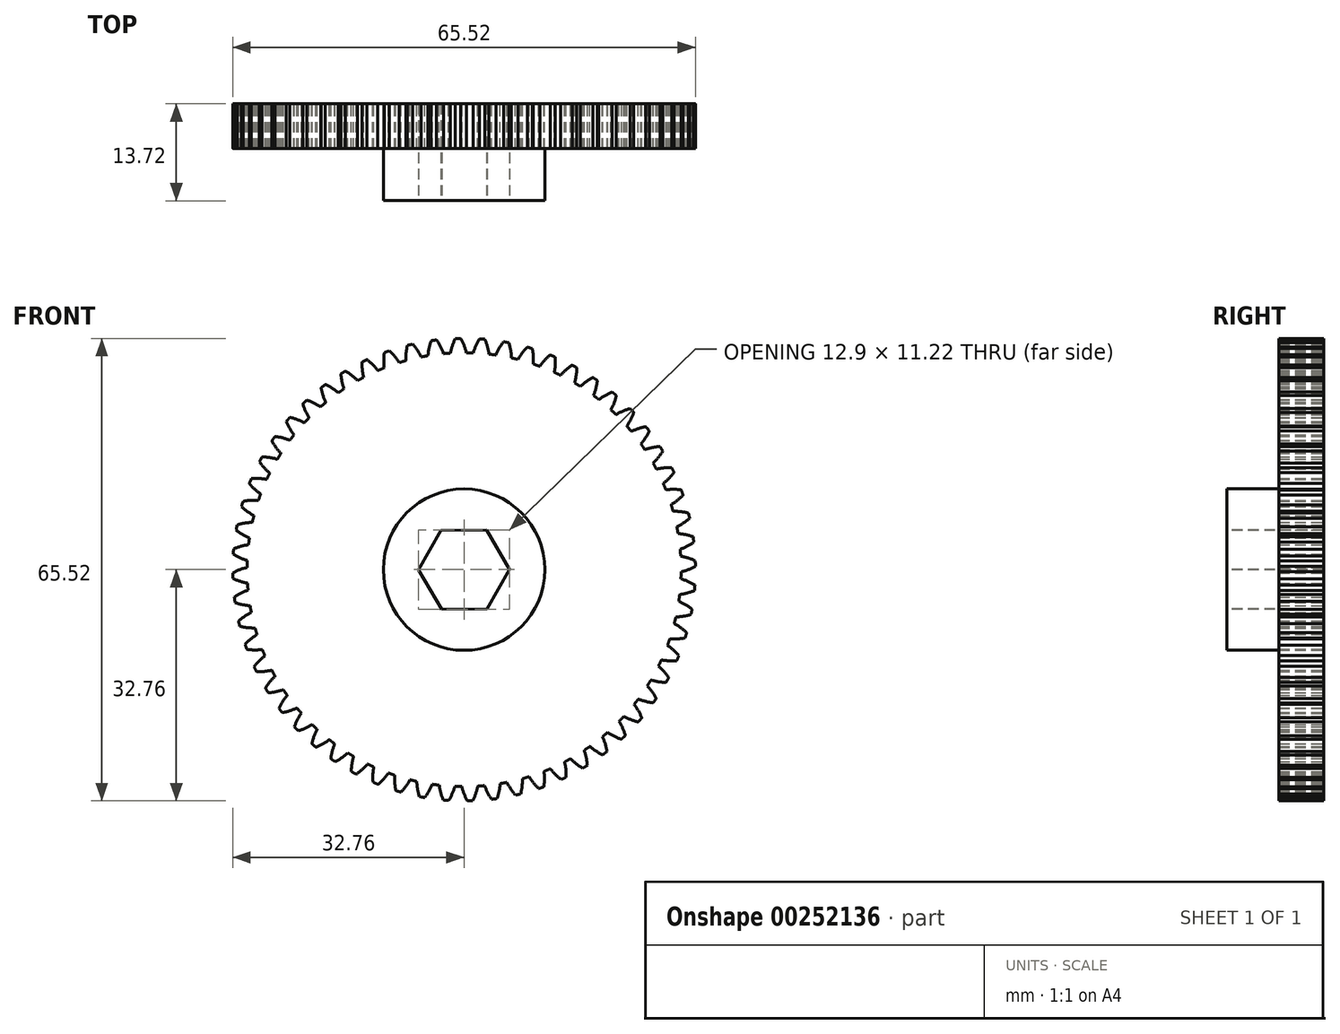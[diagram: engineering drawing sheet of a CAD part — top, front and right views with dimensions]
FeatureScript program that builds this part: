
annotation { "Feature Type Name" : "Feature", "Feature Type Description" : "" }
export const myFeature = defineFeature(function(context is Context, id is Id, definition is map)
    precondition{}
    {
        {
            var Q0;
            Q0=qCreatedBy(makeId("Front.planeOp"),FACE);
            var sketch = newSketch(context, id + "F0", { "sketchPlane" : qUnion([Q0])});
            skArc(sketch, "E0", {"start": v(-0.47, 32.76) * mm, "mid": v(-0.67, 32.76) * mm, "end": v(-0.86, 32.75) * mm});
            skArc(sketch, "E1", {"start": v(1.3, 30.7) * mm, "mid": v(0.8, 30.72) * mm, "end": v(0.31, 30.73) * mm});
            skArc(sketch, "E2.trimOffspring", {"start": v(0.31, 30.73) * mm, "mid": v(0, 31.77) * mm, "end": v(-0.47, 32.76) * mm});
            skArc(sketch, "E3.MirrorCS", {"start": v(-1.24, 32.74) * mm, "mid": v(-1.05, 32.75) * mm, "end": v(-0.86, 32.75) * mm});
            skArc(sketch, "E4.MirrorCS", {"start": v(-1.92, 30.67) * mm, "mid": v(-1.65, 31.73) * mm, "end": v(-1.24, 32.74) * mm});
            skArc(sketch, "E5.1.0", {"start": v(-5.12, 30.3) * mm, "mid": v(-4.96, 31.38) * mm, "end": v(-4.66, 32.43) * mm});
            skArc(sketch, "E5.1.1", {"start": v(-4.66, 32.43) * mm, "mid": v(-4.47, 32.46) * mm, "end": v(-4.28, 32.49) * mm});
            skArc(sketch, "E5.1.2", {"start": v(-3.9, 32.53) * mm, "mid": v(-4.09, 32.51) * mm, "end": v(-4.28, 32.49) * mm});
            skArc(sketch, "E5.1.3", {"start": v(-2.9, 30.6) * mm, "mid": v(-3.33, 31.6) * mm, "end": v(-3.9, 32.53) * mm});
            skArc(sketch, "E5.2.0", {"start": v(-8.26, 29.6) * mm, "mid": v(-8.21, 30.7) * mm, "end": v(-8.02, 31.77) * mm});
            skArc(sketch, "E5.2.1", {"start": v(-8.02, 31.77) * mm, "mid": v(-7.84, 31.82) * mm, "end": v(-7.65, 31.86) * mm});
            skArc(sketch, "E5.2.2", {"start": v(-7.28, 31.95) * mm, "mid": v(-7.46, 31.9) * mm, "end": v(-7.65, 31.86) * mm});
            skArc(sketch, "E5.2.3", {"start": v(-6.08, 30.13) * mm, "mid": v(-6.62, 31.08) * mm, "end": v(-7.28, 31.95) * mm});
            skArc(sketch, "E5.3.0", {"start": v(-11.3, 28.58) * mm, "mid": v(-11.38, 29.67) * mm, "end": v(-11.3, 30.76) * mm});
            skArc(sketch, "E5.3.1", {"start": v(-11.3, 30.76) * mm, "mid": v(-11.12, 30.82) * mm, "end": v(-10.94, 30.89) * mm});
            skArc(sketch, "E5.3.2", {"start": v(-10.57, 31.01) * mm, "mid": v(-10.76, 30.95) * mm, "end": v(-10.94, 30.89) * mm});
            skArc(sketch, "E5.3.3", {"start": v(-9.2, 29.33) * mm, "mid": v(-9.83, 30.22) * mm, "end": v(-10.57, 31.01) * mm});
            skArc(sketch, "E5.4.0", {"start": v(-14.23, 27.24) * mm, "mid": v(-14.42, 28.32) * mm, "end": v(-14.45, 29.4) * mm});
            skArc(sketch, "E5.4.1", {"start": v(-14.45, 29.4) * mm, "mid": v(-14.28, 29.5) * mm, "end": v(-14.1, 29.57) * mm});
            skArc(sketch, "E5.4.2", {"start": v(-13.76, 29.74) * mm, "mid": v(-13.93, 29.66) * mm, "end": v(-14.1, 29.57) * mm});
            skArc(sketch, "E5.4.3", {"start": v(-12.21, 28.2) * mm, "mid": v(-12.93, 29.02) * mm, "end": v(-13.76, 29.74) * mm});
            skArc(sketch, "E5.5.0", {"start": v(-17, 25.6) * mm, "mid": v(-17.3, 26.65) * mm, "end": v(-17.45, 27.74) * mm});
            skArc(sketch, "E5.5.1", {"start": v(-17.45, 27.74) * mm, "mid": v(-17.28, 27.84) * mm, "end": v(-17.12, 27.94) * mm});
            skArc(sketch, "E5.5.2", {"start": v(-16.8, 28.14) * mm, "mid": v(-16.96, 28.04) * mm, "end": v(-17.12, 27.94) * mm});
            skArc(sketch, "E5.5.3", {"start": v(-15.1, 26.77) * mm, "mid": v(-15.9, 27.51) * mm, "end": v(-16.8, 28.14) * mm});
            skArc(sketch, "E5.6.0", {"start": v(-19.59, 23.69) * mm, "mid": v(-19.99, 24.7) * mm, "end": v(-20.25, 25.76) * mm});
            skArc(sketch, "E5.6.1", {"start": v(-20.25, 25.76) * mm, "mid": v(-20.1, 25.88) * mm, "end": v(-19.95, 26) * mm});
            skArc(sketch, "E5.6.2", {"start": v(-19.64, 26.23) * mm, "mid": v(-19.8, 26.11) * mm, "end": v(-19.95, 26) * mm});
            skArc(sketch, "E5.6.3", {"start": v(-17.8, 25.05) * mm, "mid": v(-18.68, 25.7) * mm, "end": v(-19.64, 26.23) * mm});
            skArc(sketch, "E5.7.0", {"start": v(-21.95, 21.5) * mm, "mid": v(-22.46, 22.47) * mm, "end": v(-22.83, 23.5) * mm});
            skArc(sketch, "E5.7.1", {"start": v(-22.83, 23.5) * mm, "mid": v(-22.7, 23.64) * mm, "end": v(-22.55, 23.77) * mm});
            skArc(sketch, "E5.7.2", {"start": v(-22.27, 24.03) * mm, "mid": v(-22.41, 23.9) * mm, "end": v(-22.55, 23.77) * mm});
            skArc(sketch, "E5.7.3", {"start": v(-20.33, 23.05) * mm, "mid": v(-21.27, 23.6) * mm, "end": v(-22.27, 24.03) * mm});
            skArc(sketch, "E5.8.0", {"start": v(-24.08, 19.1) * mm, "mid": v(-24.69, 20) * mm, "end": v(-25.16, 20.99) * mm});
            skArc(sketch, "E5.8.1", {"start": v(-25.16, 20.99) * mm, "mid": v(-25.04, 21.13) * mm, "end": v(-24.92, 21.28) * mm});
            skArc(sketch, "E5.8.2", {"start": v(-24.66, 21.57) * mm, "mid": v(-24.8, 21.43) * mm, "end": v(-24.92, 21.28) * mm});
            skArc(sketch, "E5.8.3", {"start": v(-22.63, 20.8) * mm, "mid": v(-23.62, 21.25) * mm, "end": v(-24.66, 21.57) * mm});
            skArc(sketch, "E5.9.0", {"start": v(-25.95, 16.47) * mm, "mid": v(-26.64, 17.31) * mm, "end": v(-27.22, 18.24) * mm});
            skArc(sketch, "E5.9.1", {"start": v(-27.22, 18.24) * mm, "mid": v(-27.11, 18.4) * mm, "end": v(-27, 18.56) * mm});
            skArc(sketch, "E5.9.2", {"start": v(-26.78, 18.87) * mm, "mid": v(-26.9, 18.72) * mm, "end": v(-27, 18.56) * mm});
            skArc(sketch, "E5.9.3", {"start": v(-24.68, 18.32) * mm, "mid": v(-25.71, 18.67) * mm, "end": v(-26.78, 18.87) * mm});
            skArc(sketch, "E5.10.0", {"start": v(-27.53, 13.67) * mm, "mid": v(-28.3, 14.43) * mm, "end": v(-28.98, 15.3) * mm});
            skArc(sketch, "E5.10.1", {"start": v(-28.98, 15.3) * mm, "mid": v(-28.89, 15.47) * mm, "end": v(-28.8, 15.63) * mm});
            skArc(sketch, "E5.10.2", {"start": v(-28.61, 15.97) * mm, "mid": v(-28.7, 15.8) * mm, "end": v(-28.8, 15.63) * mm});
            skArc(sketch, "E5.10.3", {"start": v(-26.46, 15.64) * mm, "mid": v(-27.52, 15.88) * mm, "end": v(-28.61, 15.97) * mm});
            skArc(sketch, "E5.11.0", {"start": v(-28.8, 10.72) * mm, "mid": v(-29.66, 11.4) * mm, "end": v(-30.42, 12.18) * mm});
            skArc(sketch, "E5.11.1", {"start": v(-30.42, 12.18) * mm, "mid": v(-30.34, 12.36) * mm, "end": v(-30.27, 12.54) * mm});
            skArc(sketch, "E5.11.2", {"start": v(-30.12, 12.9) * mm, "mid": v(-30.2, 12.72) * mm, "end": v(-30.27, 12.54) * mm});
            skArc(sketch, "E5.11.3", {"start": v(-27.95, 12.79) * mm, "mid": v(-29.03, 12.92) * mm, "end": v(-30.12, 12.9) * mm});
            skArc(sketch, "E5.12.0", {"start": v(-29.77, 7.65) * mm, "mid": v(-30.69, 8.23) * mm, "end": v(-31.52, 8.94) * mm});
            skArc(sketch, "E5.12.1", {"start": v(-31.52, 8.94) * mm, "mid": v(-31.47, 9.12) * mm, "end": v(-31.42, 9.3) * mm});
            skArc(sketch, "E5.12.2", {"start": v(-31.3, 9.67) * mm, "mid": v(-31.36, 9.49) * mm, "end": v(-31.42, 9.3) * mm});
            skArc(sketch, "E5.12.3", {"start": v(-29.13, 9.8) * mm, "mid": v(-30.22, 9.8) * mm, "end": v(-31.3, 9.67) * mm});
            skArc(sketch, "E5.13.0", {"start": v(-30.4, 4.5) * mm, "mid": v(-31.38, 4.98) * mm, "end": v(-32.29, 5.6) * mm});
            skArc(sketch, "E5.13.1", {"start": v(-32.29, 5.6) * mm, "mid": v(-32.25, 5.78) * mm, "end": v(-32.22, 5.97) * mm});
            skArc(sketch, "E5.13.2", {"start": v(-32.15, 6.35) * mm, "mid": v(-32.18, 6.16) * mm, "end": v(-32.22, 5.97) * mm});
            skArc(sketch, "E5.13.3", {"start": v(-30, 6.7) * mm, "mid": v(-31.08, 6.6) * mm, "end": v(-32.15, 6.35) * mm});
            skArc(sketch, "E5.14.0", {"start": v(-30.7, 1.3) * mm, "mid": v(-31.73, 1.67) * mm, "end": v(-32.7, 2.19) * mm});
            skArc(sketch, "E5.14.1", {"start": v(-32.7, 2.19) * mm, "mid": v(-32.68, 2.38) * mm, "end": v(-32.66, 2.57) * mm});
            skArc(sketch, "E5.14.2", {"start": v(-32.63, 2.95) * mm, "mid": v(-32.65, 2.76) * mm, "end": v(-32.66, 2.57) * mm});
            skArc(sketch, "E5.14.3", {"start": v(-30.53, 3.53) * mm, "mid": v(-31.6, 3.31) * mm, "end": v(-32.63, 2.95) * mm});
            skArc(sketch, "E5.15.0", {"start": v(-30.67, -1.92) * mm, "mid": v(-31.73, -1.65) * mm, "end": v(-32.74, -1.24) * mm});
            skArc(sketch, "E5.15.1", {"start": v(-32.74, -1.24) * mm, "mid": v(-32.75, -1.05) * mm, "end": v(-32.75, -0.86) * mm});
            skArc(sketch, "E5.15.2", {"start": v(-32.76, -0.47) * mm, "mid": v(-32.76, -0.67) * mm, "end": v(-32.75, -0.86) * mm});
            skArc(sketch, "E5.15.3", {"start": v(-30.73, 0.31) * mm, "mid": v(-31.77, 0) * mm, "end": v(-32.76, -0.47) * mm});
            skArc(sketch, "E5.16.0", {"start": v(-30.3, -5.12) * mm, "mid": v(-31.38, -4.96) * mm, "end": v(-32.43, -4.66) * mm});
            skArc(sketch, "E5.16.1", {"start": v(-32.43, -4.66) * mm, "mid": v(-32.46, -4.47) * mm, "end": v(-32.49, -4.28) * mm});
            skArc(sketch, "E5.16.2", {"start": v(-32.53, -3.9) * mm, "mid": v(-32.51, -4.09) * mm, "end": v(-32.49, -4.28) * mm});
            skArc(sketch, "E5.16.3", {"start": v(-30.6, -2.9) * mm, "mid": v(-31.6, -3.33) * mm, "end": v(-32.53, -3.9) * mm});
            skArc(sketch, "E5.17.0", {"start": v(-29.6, -8.26) * mm, "mid": v(-30.7, -8.21) * mm, "end": v(-31.77, -8.02) * mm});
            skArc(sketch, "E5.17.1", {"start": v(-31.77, -8.02) * mm, "mid": v(-31.82, -7.84) * mm, "end": v(-31.86, -7.65) * mm});
            skArc(sketch, "E5.17.2", {"start": v(-31.95, -7.28) * mm, "mid": v(-31.9, -7.46) * mm, "end": v(-31.86, -7.65) * mm});
            skArc(sketch, "E5.17.3", {"start": v(-30.13, -6.08) * mm, "mid": v(-31.08, -6.62) * mm, "end": v(-31.95, -7.28) * mm});
            skArc(sketch, "E5.18.0", {"start": v(-28.58, -11.3) * mm, "mid": v(-29.67, -11.38) * mm, "end": v(-30.76, -11.3) * mm});
            skArc(sketch, "E5.18.1", {"start": v(-30.76, -11.3) * mm, "mid": v(-30.82, -11.12) * mm, "end": v(-30.89, -10.94) * mm});
            skArc(sketch, "E5.18.2", {"start": v(-31.01, -10.57) * mm, "mid": v(-30.95, -10.76) * mm, "end": v(-30.89, -10.94) * mm});
            skArc(sketch, "E5.18.3", {"start": v(-29.33, -9.2) * mm, "mid": v(-30.22, -9.83) * mm, "end": v(-31.01, -10.57) * mm});
            skArc(sketch, "E5.19.0", {"start": v(-27.24, -14.23) * mm, "mid": v(-28.32, -14.42) * mm, "end": v(-29.4, -14.45) * mm});
            skArc(sketch, "E5.19.1", {"start": v(-29.4, -14.45) * mm, "mid": v(-29.5, -14.28) * mm, "end": v(-29.57, -14.1) * mm});
            skArc(sketch, "E5.19.2", {"start": v(-29.74, -13.76) * mm, "mid": v(-29.66, -13.93) * mm, "end": v(-29.57, -14.1) * mm});
            skArc(sketch, "E5.19.3", {"start": v(-28.2, -12.21) * mm, "mid": v(-29.02, -12.93) * mm, "end": v(-29.74, -13.76) * mm});
            skArc(sketch, "E5.20.0", {"start": v(-25.6, -17) * mm, "mid": v(-26.65, -17.3) * mm, "end": v(-27.74, -17.45) * mm});
            skArc(sketch, "E5.20.1", {"start": v(-27.74, -17.45) * mm, "mid": v(-27.84, -17.28) * mm, "end": v(-27.94, -17.12) * mm});
            skArc(sketch, "E5.20.2", {"start": v(-28.14, -16.8) * mm, "mid": v(-28.04, -16.96) * mm, "end": v(-27.94, -17.12) * mm});
            skArc(sketch, "E5.20.3", {"start": v(-26.77, -15.1) * mm, "mid": v(-27.51, -15.9) * mm, "end": v(-28.14, -16.8) * mm});
            skArc(sketch, "E5.21.0", {"start": v(-23.69, -19.59) * mm, "mid": v(-24.7, -19.99) * mm, "end": v(-25.76, -20.25) * mm});
            skArc(sketch, "E5.21.1", {"start": v(-25.76, -20.25) * mm, "mid": v(-25.88, -20.1) * mm, "end": v(-26, -19.95) * mm});
            skArc(sketch, "E5.21.2", {"start": v(-26.23, -19.64) * mm, "mid": v(-26.11, -19.8) * mm, "end": v(-26, -19.95) * mm});
            skArc(sketch, "E5.21.3", {"start": v(-25.05, -17.8) * mm, "mid": v(-25.7, -18.68) * mm, "end": v(-26.23, -19.64) * mm});
            skArc(sketch, "E5.22.0", {"start": v(-21.5, -21.95) * mm, "mid": v(-22.47, -22.46) * mm, "end": v(-23.5, -22.83) * mm});
            skArc(sketch, "E5.22.1", {"start": v(-23.5, -22.83) * mm, "mid": v(-23.64, -22.7) * mm, "end": v(-23.77, -22.55) * mm});
            skArc(sketch, "E5.22.2", {"start": v(-24.03, -22.27) * mm, "mid": v(-23.9, -22.41) * mm, "end": v(-23.77, -22.55) * mm});
            skArc(sketch, "E5.22.3", {"start": v(-23.05, -20.33) * mm, "mid": v(-23.6, -21.27) * mm, "end": v(-24.03, -22.27) * mm});
            skArc(sketch, "E5.23.0", {"start": v(-19.1, -24.08) * mm, "mid": v(-20, -24.69) * mm, "end": v(-20.99, -25.16) * mm});
            skArc(sketch, "E5.23.1", {"start": v(-20.99, -25.16) * mm, "mid": v(-21.13, -25.04) * mm, "end": v(-21.28, -24.92) * mm});
            skArc(sketch, "E5.23.2", {"start": v(-21.57, -24.66) * mm, "mid": v(-21.43, -24.8) * mm, "end": v(-21.28, -24.92) * mm});
            skArc(sketch, "E5.23.3", {"start": v(-20.8, -22.63) * mm, "mid": v(-21.25, -23.62) * mm, "end": v(-21.57, -24.66) * mm});
            skArc(sketch, "E5.24.0", {"start": v(-16.47, -25.95) * mm, "mid": v(-17.31, -26.64) * mm, "end": v(-18.24, -27.22) * mm});
            skArc(sketch, "E5.24.1", {"start": v(-18.24, -27.22) * mm, "mid": v(-18.4, -27.11) * mm, "end": v(-18.56, -27) * mm});
            skArc(sketch, "E5.24.2", {"start": v(-18.87, -26.78) * mm, "mid": v(-18.72, -26.9) * mm, "end": v(-18.56, -27) * mm});
            skArc(sketch, "E5.24.3", {"start": v(-18.32, -24.68) * mm, "mid": v(-18.67, -25.71) * mm, "end": v(-18.87, -26.78) * mm});
            skArc(sketch, "E5.25.0", {"start": v(-13.67, -27.53) * mm, "mid": v(-14.43, -28.3) * mm, "end": v(-15.3, -28.98) * mm});
            skArc(sketch, "E5.25.1", {"start": v(-15.3, -28.98) * mm, "mid": v(-15.47, -28.89) * mm, "end": v(-15.63, -28.8) * mm});
            skArc(sketch, "E5.25.2", {"start": v(-15.97, -28.61) * mm, "mid": v(-15.8, -28.7) * mm, "end": v(-15.63, -28.8) * mm});
            skArc(sketch, "E5.25.3", {"start": v(-15.64, -26.46) * mm, "mid": v(-15.88, -27.52) * mm, "end": v(-15.97, -28.61) * mm});
            skArc(sketch, "E5.26.0", {"start": v(-10.72, -28.8) * mm, "mid": v(-11.4, -29.66) * mm, "end": v(-12.18, -30.42) * mm});
            skArc(sketch, "E5.26.1", {"start": v(-12.18, -30.42) * mm, "mid": v(-12.36, -30.34) * mm, "end": v(-12.54, -30.27) * mm});
            skArc(sketch, "E5.26.2", {"start": v(-12.9, -30.12) * mm, "mid": v(-12.72, -30.2) * mm, "end": v(-12.54, -30.27) * mm});
            skArc(sketch, "E5.26.3", {"start": v(-12.79, -27.95) * mm, "mid": v(-12.92, -29.03) * mm, "end": v(-12.9, -30.12) * mm});
            skArc(sketch, "E5.27.0", {"start": v(-7.65, -29.77) * mm, "mid": v(-8.23, -30.69) * mm, "end": v(-8.94, -31.52) * mm});
            skArc(sketch, "E5.27.1", {"start": v(-8.94, -31.52) * mm, "mid": v(-9.12, -31.47) * mm, "end": v(-9.3, -31.42) * mm});
            skArc(sketch, "E5.27.2", {"start": v(-9.67, -31.3) * mm, "mid": v(-9.49, -31.36) * mm, "end": v(-9.3, -31.42) * mm});
            skArc(sketch, "E5.27.3", {"start": v(-9.8, -29.13) * mm, "mid": v(-9.8, -30.22) * mm, "end": v(-9.67, -31.3) * mm});
            skArc(sketch, "E5.28.0", {"start": v(-4.5, -30.4) * mm, "mid": v(-4.98, -31.38) * mm, "end": v(-5.6, -32.29) * mm});
            skArc(sketch, "E5.28.1", {"start": v(-5.6, -32.29) * mm, "mid": v(-5.78, -32.25) * mm, "end": v(-5.97, -32.22) * mm});
            skArc(sketch, "E5.28.2", {"start": v(-6.35, -32.15) * mm, "mid": v(-6.16, -32.18) * mm, "end": v(-5.97, -32.22) * mm});
            skArc(sketch, "E5.28.3", {"start": v(-6.7, -30) * mm, "mid": v(-6.6, -31.08) * mm, "end": v(-6.35, -32.15) * mm});
            skArc(sketch, "E5.29.0", {"start": v(-1.3, -30.7) * mm, "mid": v(-1.67, -31.73) * mm, "end": v(-2.19, -32.7) * mm});
            skArc(sketch, "E5.29.1", {"start": v(-2.19, -32.7) * mm, "mid": v(-2.38, -32.68) * mm, "end": v(-2.57, -32.66) * mm});
            skArc(sketch, "E5.29.2", {"start": v(-2.95, -32.63) * mm, "mid": v(-2.76, -32.65) * mm, "end": v(-2.57, -32.66) * mm});
            skArc(sketch, "E5.29.3", {"start": v(-3.53, -30.53) * mm, "mid": v(-3.31, -31.6) * mm, "end": v(-2.95, -32.63) * mm});
            skArc(sketch, "E5.30.0", {"start": v(1.92, -30.67) * mm, "mid": v(1.65, -31.73) * mm, "end": v(1.24, -32.74) * mm});
            skArc(sketch, "E5.30.1", {"start": v(1.24, -32.74) * mm, "mid": v(1.05, -32.75) * mm, "end": v(0.86, -32.75) * mm});
            skArc(sketch, "E5.30.2", {"start": v(0.47, -32.76) * mm, "mid": v(0.67, -32.76) * mm, "end": v(0.86, -32.75) * mm});
            skArc(sketch, "E5.30.3", {"start": v(-0.31, -30.73) * mm, "mid": v(0, -31.77) * mm, "end": v(0.47, -32.76) * mm});
            skArc(sketch, "E5.31.0", {"start": v(5.12, -30.3) * mm, "mid": v(4.96, -31.38) * mm, "end": v(4.66, -32.43) * mm});
            skArc(sketch, "E5.31.1", {"start": v(4.66, -32.43) * mm, "mid": v(4.47, -32.46) * mm, "end": v(4.28, -32.49) * mm});
            skArc(sketch, "E5.31.2", {"start": v(3.9, -32.53) * mm, "mid": v(4.09, -32.51) * mm, "end": v(4.28, -32.49) * mm});
            skArc(sketch, "E5.31.3", {"start": v(2.9, -30.6) * mm, "mid": v(3.33, -31.6) * mm, "end": v(3.9, -32.53) * mm});
            skArc(sketch, "E5.32.0", {"start": v(8.26, -29.6) * mm, "mid": v(8.21, -30.7) * mm, "end": v(8.02, -31.77) * mm});
            skArc(sketch, "E5.32.1", {"start": v(8.02, -31.77) * mm, "mid": v(7.84, -31.82) * mm, "end": v(7.65, -31.86) * mm});
            skArc(sketch, "E5.32.2", {"start": v(7.28, -31.95) * mm, "mid": v(7.46, -31.9) * mm, "end": v(7.65, -31.86) * mm});
            skArc(sketch, "E5.32.3", {"start": v(6.08, -30.13) * mm, "mid": v(6.62, -31.08) * mm, "end": v(7.28, -31.95) * mm});
            skArc(sketch, "E5.33.0", {"start": v(11.3, -28.58) * mm, "mid": v(11.38, -29.67) * mm, "end": v(11.3, -30.76) * mm});
            skArc(sketch, "E5.33.1", {"start": v(11.3, -30.76) * mm, "mid": v(11.12, -30.82) * mm, "end": v(10.94, -30.89) * mm});
            skArc(sketch, "E5.33.2", {"start": v(10.57, -31.01) * mm, "mid": v(10.76, -30.95) * mm, "end": v(10.94, -30.89) * mm});
            skArc(sketch, "E5.33.3", {"start": v(9.2, -29.33) * mm, "mid": v(9.83, -30.22) * mm, "end": v(10.57, -31.01) * mm});
            skArc(sketch, "E5.34.0", {"start": v(14.23, -27.24) * mm, "mid": v(14.42, -28.32) * mm, "end": v(14.45, -29.4) * mm});
            skArc(sketch, "E5.34.1", {"start": v(14.45, -29.4) * mm, "mid": v(14.28, -29.5) * mm, "end": v(14.1, -29.57) * mm});
            skArc(sketch, "E5.34.2", {"start": v(13.76, -29.74) * mm, "mid": v(13.93, -29.66) * mm, "end": v(14.1, -29.57) * mm});
            skArc(sketch, "E5.34.3", {"start": v(12.21, -28.2) * mm, "mid": v(12.93, -29.02) * mm, "end": v(13.76, -29.74) * mm});
            skArc(sketch, "E5.35.0", {"start": v(17, -25.6) * mm, "mid": v(17.3, -26.65) * mm, "end": v(17.45, -27.74) * mm});
            skArc(sketch, "E5.35.1", {"start": v(17.45, -27.74) * mm, "mid": v(17.28, -27.84) * mm, "end": v(17.12, -27.94) * mm});
            skArc(sketch, "E5.35.2", {"start": v(16.8, -28.14) * mm, "mid": v(16.96, -28.04) * mm, "end": v(17.12, -27.94) * mm});
            skArc(sketch, "E5.35.3", {"start": v(15.1, -26.77) * mm, "mid": v(15.9, -27.51) * mm, "end": v(16.8, -28.14) * mm});
            skArc(sketch, "E5.36.0", {"start": v(19.59, -23.69) * mm, "mid": v(19.99, -24.7) * mm, "end": v(20.25, -25.76) * mm});
            skArc(sketch, "E5.36.1", {"start": v(20.25, -25.76) * mm, "mid": v(20.1, -25.88) * mm, "end": v(19.95, -26) * mm});
            skArc(sketch, "E5.36.2", {"start": v(19.64, -26.23) * mm, "mid": v(19.8, -26.11) * mm, "end": v(19.95, -26) * mm});
            skArc(sketch, "E5.36.3", {"start": v(17.8, -25.05) * mm, "mid": v(18.68, -25.7) * mm, "end": v(19.64, -26.23) * mm});
            skArc(sketch, "E5.37.0", {"start": v(21.95, -21.5) * mm, "mid": v(22.46, -22.47) * mm, "end": v(22.83, -23.5) * mm});
            skArc(sketch, "E5.37.1", {"start": v(22.83, -23.5) * mm, "mid": v(22.7, -23.64) * mm, "end": v(22.55, -23.77) * mm});
            skArc(sketch, "E5.37.2", {"start": v(22.27, -24.03) * mm, "mid": v(22.41, -23.9) * mm, "end": v(22.55, -23.77) * mm});
            skArc(sketch, "E5.37.3", {"start": v(20.33, -23.05) * mm, "mid": v(21.27, -23.6) * mm, "end": v(22.27, -24.03) * mm});
            skArc(sketch, "E5.38.0", {"start": v(24.08, -19.1) * mm, "mid": v(24.69, -20) * mm, "end": v(25.16, -20.99) * mm});
            skArc(sketch, "E5.38.1", {"start": v(25.16, -20.99) * mm, "mid": v(25.04, -21.13) * mm, "end": v(24.92, -21.28) * mm});
            skArc(sketch, "E5.38.2", {"start": v(24.66, -21.57) * mm, "mid": v(24.8, -21.43) * mm, "end": v(24.92, -21.28) * mm});
            skArc(sketch, "E5.38.3", {"start": v(22.63, -20.8) * mm, "mid": v(23.62, -21.25) * mm, "end": v(24.66, -21.57) * mm});
            skArc(sketch, "E5.39.0", {"start": v(25.95, -16.47) * mm, "mid": v(26.64, -17.31) * mm, "end": v(27.22, -18.24) * mm});
            skArc(sketch, "E5.39.1", {"start": v(27.22, -18.24) * mm, "mid": v(27.11, -18.4) * mm, "end": v(27, -18.56) * mm});
            skArc(sketch, "E5.39.2", {"start": v(26.78, -18.87) * mm, "mid": v(26.9, -18.72) * mm, "end": v(27, -18.56) * mm});
            skArc(sketch, "E5.39.3", {"start": v(24.68, -18.32) * mm, "mid": v(25.71, -18.67) * mm, "end": v(26.78, -18.87) * mm});
            skArc(sketch, "E5.40.0", {"start": v(27.53, -13.67) * mm, "mid": v(28.3, -14.43) * mm, "end": v(28.98, -15.3) * mm});
            skArc(sketch, "E5.40.1", {"start": v(28.98, -15.3) * mm, "mid": v(28.89, -15.47) * mm, "end": v(28.8, -15.63) * mm});
            skArc(sketch, "E5.40.2", {"start": v(28.61, -15.97) * mm, "mid": v(28.7, -15.8) * mm, "end": v(28.8, -15.63) * mm});
            skArc(sketch, "E5.40.3", {"start": v(26.46, -15.64) * mm, "mid": v(27.52, -15.88) * mm, "end": v(28.61, -15.97) * mm});
            skArc(sketch, "E5.41.0", {"start": v(28.8, -10.72) * mm, "mid": v(29.66, -11.4) * mm, "end": v(30.42, -12.18) * mm});
            skArc(sketch, "E5.41.1", {"start": v(30.42, -12.18) * mm, "mid": v(30.34, -12.36) * mm, "end": v(30.27, -12.54) * mm});
            skArc(sketch, "E5.41.2", {"start": v(30.12, -12.9) * mm, "mid": v(30.2, -12.72) * mm, "end": v(30.27, -12.54) * mm});
            skArc(sketch, "E5.41.3", {"start": v(27.95, -12.79) * mm, "mid": v(29.03, -12.92) * mm, "end": v(30.12, -12.9) * mm});
            skArc(sketch, "E5.42.0", {"start": v(29.77, -7.65) * mm, "mid": v(30.69, -8.23) * mm, "end": v(31.52, -8.94) * mm});
            skArc(sketch, "E5.42.1", {"start": v(31.52, -8.94) * mm, "mid": v(31.47, -9.12) * mm, "end": v(31.42, -9.3) * mm});
            skArc(sketch, "E5.42.2", {"start": v(31.3, -9.67) * mm, "mid": v(31.36, -9.49) * mm, "end": v(31.42, -9.3) * mm});
            skArc(sketch, "E5.42.3", {"start": v(29.13, -9.8) * mm, "mid": v(30.22, -9.8) * mm, "end": v(31.3, -9.67) * mm});
            skArc(sketch, "E5.43.0", {"start": v(30.4, -4.5) * mm, "mid": v(31.38, -4.98) * mm, "end": v(32.29, -5.6) * mm});
            skArc(sketch, "E5.43.1", {"start": v(32.29, -5.6) * mm, "mid": v(32.25, -5.78) * mm, "end": v(32.22, -5.97) * mm});
            skArc(sketch, "E5.43.2", {"start": v(32.15, -6.35) * mm, "mid": v(32.18, -6.16) * mm, "end": v(32.22, -5.97) * mm});
            skArc(sketch, "E5.43.3", {"start": v(30, -6.7) * mm, "mid": v(31.08, -6.6) * mm, "end": v(32.15, -6.35) * mm});
            skArc(sketch, "E5.44.0", {"start": v(30.7, -1.3) * mm, "mid": v(31.73, -1.67) * mm, "end": v(32.7, -2.19) * mm});
            skArc(sketch, "E5.44.1", {"start": v(32.7, -2.19) * mm, "mid": v(32.68, -2.38) * mm, "end": v(32.66, -2.57) * mm});
            skArc(sketch, "E5.44.2", {"start": v(32.63, -2.95) * mm, "mid": v(32.65, -2.76) * mm, "end": v(32.66, -2.57) * mm});
            skArc(sketch, "E5.44.3", {"start": v(30.53, -3.53) * mm, "mid": v(31.6, -3.31) * mm, "end": v(32.63, -2.95) * mm});
            skArc(sketch, "E5.45.0", {"start": v(30.67, 1.92) * mm, "mid": v(31.73, 1.65) * mm, "end": v(32.74, 1.24) * mm});
            skArc(sketch, "E5.45.1", {"start": v(32.74, 1.24) * mm, "mid": v(32.75, 1.05) * mm, "end": v(32.75, 0.86) * mm});
            skArc(sketch, "E5.45.2", {"start": v(32.76, 0.47) * mm, "mid": v(32.76, 0.67) * mm, "end": v(32.75, 0.86) * mm});
            skArc(sketch, "E5.45.3", {"start": v(30.73, -0.31) * mm, "mid": v(31.77, 0) * mm, "end": v(32.76, 0.47) * mm});
            skArc(sketch, "E5.46.0", {"start": v(30.3, 5.12) * mm, "mid": v(31.38, 4.96) * mm, "end": v(32.43, 4.66) * mm});
            skArc(sketch, "E5.46.1", {"start": v(32.43, 4.66) * mm, "mid": v(32.46, 4.47) * mm, "end": v(32.49, 4.28) * mm});
            skArc(sketch, "E5.46.2", {"start": v(32.53, 3.9) * mm, "mid": v(32.51, 4.09) * mm, "end": v(32.49, 4.28) * mm});
            skArc(sketch, "E5.46.3", {"start": v(30.6, 2.9) * mm, "mid": v(31.6, 3.33) * mm, "end": v(32.53, 3.9) * mm});
            skArc(sketch, "E5.47.0", {"start": v(29.6, 8.26) * mm, "mid": v(30.7, 8.21) * mm, "end": v(31.77, 8.02) * mm});
            skArc(sketch, "E5.47.1", {"start": v(31.77, 8.02) * mm, "mid": v(31.82, 7.84) * mm, "end": v(31.86, 7.65) * mm});
            skArc(sketch, "E5.47.2", {"start": v(31.95, 7.28) * mm, "mid": v(31.9, 7.46) * mm, "end": v(31.86, 7.65) * mm});
            skArc(sketch, "E5.47.3", {"start": v(30.13, 6.08) * mm, "mid": v(31.08, 6.62) * mm, "end": v(31.95, 7.28) * mm});
            skArc(sketch, "E5.48.0", {"start": v(28.58, 11.3) * mm, "mid": v(29.67, 11.38) * mm, "end": v(30.76, 11.3) * mm});
            skArc(sketch, "E5.48.1", {"start": v(30.76, 11.3) * mm, "mid": v(30.82, 11.12) * mm, "end": v(30.89, 10.94) * mm});
            skArc(sketch, "E5.48.2", {"start": v(31.01, 10.57) * mm, "mid": v(30.95, 10.76) * mm, "end": v(30.89, 10.94) * mm});
            skArc(sketch, "E5.48.3", {"start": v(29.33, 9.2) * mm, "mid": v(30.22, 9.83) * mm, "end": v(31.01, 10.57) * mm});
            skArc(sketch, "E5.49.0", {"start": v(27.24, 14.23) * mm, "mid": v(28.32, 14.42) * mm, "end": v(29.4, 14.45) * mm});
            skArc(sketch, "E5.49.1", {"start": v(29.4, 14.45) * mm, "mid": v(29.5, 14.28) * mm, "end": v(29.57, 14.1) * mm});
            skArc(sketch, "E5.49.2", {"start": v(29.74, 13.76) * mm, "mid": v(29.66, 13.93) * mm, "end": v(29.57, 14.1) * mm});
            skArc(sketch, "E5.49.3", {"start": v(28.2, 12.21) * mm, "mid": v(29.02, 12.93) * mm, "end": v(29.74, 13.76) * mm});
            skArc(sketch, "E5.50.0", {"start": v(25.6, 17) * mm, "mid": v(26.65, 17.3) * mm, "end": v(27.74, 17.45) * mm});
            skArc(sketch, "E5.50.1", {"start": v(27.74, 17.45) * mm, "mid": v(27.84, 17.28) * mm, "end": v(27.94, 17.12) * mm});
            skArc(sketch, "E5.50.2", {"start": v(28.14, 16.8) * mm, "mid": v(28.04, 16.96) * mm, "end": v(27.94, 17.12) * mm});
            skArc(sketch, "E5.50.3", {"start": v(26.77, 15.1) * mm, "mid": v(27.51, 15.9) * mm, "end": v(28.14, 16.8) * mm});
            skArc(sketch, "E5.51.0", {"start": v(23.69, 19.59) * mm, "mid": v(24.7, 19.99) * mm, "end": v(25.76, 20.25) * mm});
            skArc(sketch, "E5.51.1", {"start": v(25.76, 20.25) * mm, "mid": v(25.88, 20.1) * mm, "end": v(26, 19.95) * mm});
            skArc(sketch, "E5.51.2", {"start": v(26.23, 19.64) * mm, "mid": v(26.11, 19.8) * mm, "end": v(26, 19.95) * mm});
            skArc(sketch, "E5.51.3", {"start": v(25.05, 17.8) * mm, "mid": v(25.7, 18.68) * mm, "end": v(26.23, 19.64) * mm});
            skArc(sketch, "E5.52.0", {"start": v(21.5, 21.95) * mm, "mid": v(22.47, 22.46) * mm, "end": v(23.5, 22.83) * mm});
            skArc(sketch, "E5.52.1", {"start": v(23.5, 22.83) * mm, "mid": v(23.64, 22.7) * mm, "end": v(23.77, 22.55) * mm});
            skArc(sketch, "E5.52.2", {"start": v(24.03, 22.27) * mm, "mid": v(23.9, 22.41) * mm, "end": v(23.77, 22.55) * mm});
            skArc(sketch, "E5.52.3", {"start": v(23.05, 20.33) * mm, "mid": v(23.6, 21.27) * mm, "end": v(24.03, 22.27) * mm});
            skArc(sketch, "E5.53.0", {"start": v(19.1, 24.08) * mm, "mid": v(20, 24.69) * mm, "end": v(20.99, 25.16) * mm});
            skArc(sketch, "E5.53.1", {"start": v(20.99, 25.16) * mm, "mid": v(21.13, 25.04) * mm, "end": v(21.28, 24.92) * mm});
            skArc(sketch, "E5.53.2", {"start": v(21.57, 24.66) * mm, "mid": v(21.43, 24.8) * mm, "end": v(21.28, 24.92) * mm});
            skArc(sketch, "E5.53.3", {"start": v(20.8, 22.63) * mm, "mid": v(21.25, 23.62) * mm, "end": v(21.57, 24.66) * mm});
            skArc(sketch, "E5.54.0", {"start": v(16.47, 25.95) * mm, "mid": v(17.31, 26.64) * mm, "end": v(18.24, 27.22) * mm});
            skArc(sketch, "E5.54.1", {"start": v(18.24, 27.22) * mm, "mid": v(18.4, 27.11) * mm, "end": v(18.56, 27) * mm});
            skArc(sketch, "E5.54.2", {"start": v(18.87, 26.78) * mm, "mid": v(18.72, 26.9) * mm, "end": v(18.56, 27) * mm});
            skArc(sketch, "E5.54.3", {"start": v(18.32, 24.68) * mm, "mid": v(18.67, 25.71) * mm, "end": v(18.87, 26.78) * mm});
            skArc(sketch, "E5.55.0", {"start": v(13.67, 27.53) * mm, "mid": v(14.43, 28.3) * mm, "end": v(15.3, 28.98) * mm});
            skArc(sketch, "E5.55.1", {"start": v(15.3, 28.98) * mm, "mid": v(15.47, 28.89) * mm, "end": v(15.63, 28.8) * mm});
            skArc(sketch, "E5.55.2", {"start": v(15.97, 28.61) * mm, "mid": v(15.8, 28.7) * mm, "end": v(15.63, 28.8) * mm});
            skArc(sketch, "E5.55.3", {"start": v(15.64, 26.46) * mm, "mid": v(15.88, 27.52) * mm, "end": v(15.97, 28.61) * mm});
            skArc(sketch, "E5.56.0", {"start": v(10.72, 28.8) * mm, "mid": v(11.4, 29.66) * mm, "end": v(12.18, 30.42) * mm});
            skArc(sketch, "E5.56.1", {"start": v(12.18, 30.42) * mm, "mid": v(12.36, 30.34) * mm, "end": v(12.54, 30.27) * mm});
            skArc(sketch, "E5.56.2", {"start": v(12.9, 30.12) * mm, "mid": v(12.72, 30.2) * mm, "end": v(12.54, 30.27) * mm});
            skArc(sketch, "E5.56.3", {"start": v(12.79, 27.95) * mm, "mid": v(12.92, 29.03) * mm, "end": v(12.9, 30.12) * mm});
            skArc(sketch, "E5.57.0", {"start": v(7.65, 29.77) * mm, "mid": v(8.23, 30.69) * mm, "end": v(8.94, 31.52) * mm});
            skArc(sketch, "E5.57.1", {"start": v(8.94, 31.52) * mm, "mid": v(9.12, 31.47) * mm, "end": v(9.3, 31.42) * mm});
            skArc(sketch, "E5.57.2", {"start": v(9.67, 31.3) * mm, "mid": v(9.49, 31.36) * mm, "end": v(9.3, 31.42) * mm});
            skArc(sketch, "E5.57.3", {"start": v(9.8, 29.13) * mm, "mid": v(9.8, 30.22) * mm, "end": v(9.67, 31.3) * mm});
            skArc(sketch, "E5.58.0", {"start": v(4.5, 30.4) * mm, "mid": v(4.98, 31.38) * mm, "end": v(5.6, 32.29) * mm});
            skArc(sketch, "E5.58.1", {"start": v(5.6, 32.29) * mm, "mid": v(5.78, 32.25) * mm, "end": v(5.97, 32.22) * mm});
            skArc(sketch, "E5.58.2", {"start": v(6.35, 32.15) * mm, "mid": v(6.16, 32.18) * mm, "end": v(5.97, 32.22) * mm});
            skArc(sketch, "E5.58.3", {"start": v(6.7, 30) * mm, "mid": v(6.6, 31.08) * mm, "end": v(6.35, 32.15) * mm});
            skArc(sketch, "E5.59.0", {"start": v(1.3, 30.7) * mm, "mid": v(1.67, 31.73) * mm, "end": v(2.19, 32.7) * mm});
            skArc(sketch, "E5.59.1", {"start": v(2.19, 32.7) * mm, "mid": v(2.38, 32.68) * mm, "end": v(2.57, 32.66) * mm});
            skArc(sketch, "E5.59.2", {"start": v(2.95, 32.63) * mm, "mid": v(2.76, 32.65) * mm, "end": v(2.57, 32.66) * mm});
            skArc(sketch, "E5.59.3", {"start": v(3.53, 30.53) * mm, "mid": v(3.31, 31.6) * mm, "end": v(2.95, 32.63) * mm});
            skArc(sketch, "E6.trimOffspring", {"start": v(4.5, 30.4) * mm, "mid": v(4.01, 30.47) * mm, "end": v(3.53, 30.53) * mm});
            skArc(sketch, "E7.trimOffspring", {"start": v(7.65, 29.77) * mm, "mid": v(7.17, 29.88) * mm, "end": v(6.7, 30) * mm});
            skArc(sketch, "E8.trimOffspring", {"start": v(10.72, 28.8) * mm, "mid": v(10.26, 28.97) * mm, "end": v(9.8, 29.13) * mm});
            skArc(sketch, "E9.trimOffspring", {"start": v(13.67, 27.53) * mm, "mid": v(13.23, 27.74) * mm, "end": v(12.79, 27.95) * mm});
            skArc(sketch, "E10.trimOffspring", {"start": v(16.47, 25.95) * mm, "mid": v(16.06, 26.2) * mm, "end": v(15.64, 26.46) * mm});
            skArc(sketch, "E11.trimOffspring", {"start": v(19.1, 24.08) * mm, "mid": v(18.7, 24.38) * mm, "end": v(18.32, 24.68) * mm});
            skArc(sketch, "E12.trimOffspring", {"start": v(21.5, 21.95) * mm, "mid": v(21.16, 22.3) * mm, "end": v(20.8, 22.63) * mm});
            skArc(sketch, "E13.trimOffspring", {"start": v(23.69, 19.59) * mm, "mid": v(23.37, 19.96) * mm, "end": v(23.05, 20.33) * mm});
            skArc(sketch, "E14.trimOffspring", {"start": v(25.6, 17) * mm, "mid": v(25.33, 17.4) * mm, "end": v(25.05, 17.8) * mm});
            skArc(sketch, "E15.trimOffspring", {"start": v(27.24, 14.23) * mm, "mid": v(27, 14.66) * mm, "end": v(26.77, 15.1) * mm});
            skArc(sketch, "E16.trimOffspring", {"start": v(28.58, 11.3) * mm, "mid": v(28.4, 11.76) * mm, "end": v(28.2, 12.21) * mm});
            skArc(sketch, "E17.trimOffspring", {"start": v(29.6, 8.26) * mm, "mid": v(29.47, 8.73) * mm, "end": v(29.33, 9.2) * mm});
            skArc(sketch, "E18.trimOffspring", {"start": v(30.3, 5.12) * mm, "mid": v(30.22, 5.6) * mm, "end": v(30.13, 6.08) * mm});
            skArc(sketch, "E19.trimOffspring", {"start": v(30.67, 1.92) * mm, "mid": v(30.64, 2.41) * mm, "end": v(30.6, 2.9) * mm});
            skArc(sketch, "E20.trimOffspring", {"start": v(30.7, -1.3) * mm, "mid": v(30.72, -0.8) * mm, "end": v(30.73, -0.31) * mm});
            skArc(sketch, "E21.trimOffspring", {"start": v(30.4, -4.5) * mm, "mid": v(30.47, -4.01) * mm, "end": v(30.53, -3.53) * mm});
            skArc(sketch, "E22.trimOffspring", {"start": v(29.77, -7.65) * mm, "mid": v(29.88, -7.17) * mm, "end": v(30, -6.7) * mm});
            skArc(sketch, "E23.trimOffspring", {"start": v(28.8, -10.72) * mm, "mid": v(28.97, -10.26) * mm, "end": v(29.13, -9.8) * mm});
            skArc(sketch, "E24.trimOffspring", {"start": v(24.08, -19.1) * mm, "mid": v(24.38, -18.7) * mm, "end": v(24.68, -18.32) * mm});
            skArc(sketch, "E25.trimOffspring", {"start": v(27.53, -13.67) * mm, "mid": v(27.74, -13.23) * mm, "end": v(27.95, -12.79) * mm});
            skArc(sketch, "E26.trimOffspring", {"start": v(25.95, -16.47) * mm, "mid": v(26.2, -16.06) * mm, "end": v(26.46, -15.64) * mm});
            skArc(sketch, "E27.trimOffspring", {"start": v(21.95, -21.5) * mm, "mid": v(22.3, -21.16) * mm, "end": v(22.63, -20.8) * mm});
            skArc(sketch, "E28.trimOffspring", {"start": v(19.59, -23.69) * mm, "mid": v(19.96, -23.37) * mm, "end": v(20.33, -23.05) * mm});
            skArc(sketch, "E29.trimOffspring", {"start": v(17, -25.6) * mm, "mid": v(17.4, -25.33) * mm, "end": v(17.8, -25.05) * mm});
            skArc(sketch, "E30.trimOffspring", {"start": v(14.23, -27.24) * mm, "mid": v(14.66, -27) * mm, "end": v(15.1, -26.77) * mm});
            skArc(sketch, "E31.trimOffspring", {"start": v(11.3, -28.58) * mm, "mid": v(11.76, -28.4) * mm, "end": v(12.21, -28.2) * mm});
            skLineSegment(sketch, "E32", {"start": v(8.26, -29.6) * mm, "end": v(9.2, -29.33) * mm});
            skArc(sketch, "E33.trimOffspring", {"start": v(5.12, -30.3) * mm, "mid": v(5.6, -30.22) * mm, "end": v(6.08, -30.13) * mm});
            skArc(sketch, "E34.trimOffspring", {"start": v(-1.3, -30.7) * mm, "mid": v(-0.8, -30.72) * mm, "end": v(-0.31, -30.73) * mm});
            skArc(sketch, "E35.trimOffspring", {"start": v(1.92, -30.67) * mm, "mid": v(2.41, -30.64) * mm, "end": v(2.9, -30.6) * mm});
            skArc(sketch, "E36.trimOffspring", {"start": v(-4.5, -30.4) * mm, "mid": v(-4.01, -30.47) * mm, "end": v(-3.53, -30.53) * mm});
            skArc(sketch, "E37.trimOffspring", {"start": v(-7.65, -29.77) * mm, "mid": v(-7.17, -29.88) * mm, "end": v(-6.7, -30) * mm});
            skArc(sketch, "E38.trimOffspring", {"start": v(-10.72, -28.8) * mm, "mid": v(-10.26, -28.97) * mm, "end": v(-9.8, -29.13) * mm});
            skArc(sketch, "E39.trimOffspring", {"start": v(-13.67, -27.53) * mm, "mid": v(-13.23, -27.74) * mm, "end": v(-12.79, -27.95) * mm});
            skArc(sketch, "E40.trimOffspring", {"start": v(-16.47, -25.95) * mm, "mid": v(-16.06, -26.2) * mm, "end": v(-15.64, -26.46) * mm});
            skArc(sketch, "E41.trimOffspring", {"start": v(-19.1, -24.08) * mm, "mid": v(-18.7, -24.38) * mm, "end": v(-18.32, -24.68) * mm});
            skArc(sketch, "E42.trimOffspring", {"start": v(-23.69, -19.59) * mm, "mid": v(-23.37, -19.96) * mm, "end": v(-23.05, -20.33) * mm});
            skArc(sketch, "E43.trimOffspring", {"start": v(-21.5, -21.95) * mm, "mid": v(-21.16, -22.3) * mm, "end": v(-20.8, -22.63) * mm});
            skArc(sketch, "E44.trimOffspring", {"start": v(-25.6, -17) * mm, "mid": v(-25.33, -17.4) * mm, "end": v(-25.05, -17.8) * mm});
            skArc(sketch, "E45.trimOffspring", {"start": v(-27.24, -14.23) * mm, "mid": v(-27, -14.66) * mm, "end": v(-26.77, -15.1) * mm});
            skArc(sketch, "E46.trimOffspring", {"start": v(-28.58, -11.3) * mm, "mid": v(-28.4, -11.76) * mm, "end": v(-28.2, -12.21) * mm});
            skArc(sketch, "E47.trimOffspring", {"start": v(-30.3, -5.12) * mm, "mid": v(-30.22, -5.6) * mm, "end": v(-30.13, -6.08) * mm});
            skArc(sketch, "E48.trimOffspring", {"start": v(-29.6, -8.26) * mm, "mid": v(-29.47, -8.73) * mm, "end": v(-29.33, -9.2) * mm});
            skArc(sketch, "E49.trimOffspring", {"start": v(-30.67, -1.92) * mm, "mid": v(-30.64, -2.41) * mm, "end": v(-30.6, -2.9) * mm});
            skArc(sketch, "E50.trimOffspring", {"start": v(-30.7, 1.3) * mm, "mid": v(-30.72, 0.8) * mm, "end": v(-30.73, 0.31) * mm});
            skArc(sketch, "E51.trimOffspring", {"start": v(-30.4, 4.5) * mm, "mid": v(-30.47, 4.01) * mm, "end": v(-30.53, 3.53) * mm});
            skArc(sketch, "E52.trimOffspring", {"start": v(-29.77, 7.65) * mm, "mid": v(-29.88, 7.17) * mm, "end": v(-30, 6.7) * mm});
            skArc(sketch, "E53.trimOffspring", {"start": v(-28.8, 10.72) * mm, "mid": v(-28.97, 10.26) * mm, "end": v(-29.13, 9.8) * mm});
            skArc(sketch, "E54.trimOffspring", {"start": v(-27.53, 13.67) * mm, "mid": v(-27.74, 13.23) * mm, "end": v(-27.95, 12.79) * mm});
            skArc(sketch, "E55.trimOffspring", {"start": v(-25.95, 16.47) * mm, "mid": v(-26.2, 16.06) * mm, "end": v(-26.46, 15.64) * mm});
            skArc(sketch, "E56.trimOffspring", {"start": v(-24.08, 19.1) * mm, "mid": v(-24.38, 18.7) * mm, "end": v(-24.68, 18.32) * mm});
            skArc(sketch, "E57.trimOffspring", {"start": v(-21.95, 21.5) * mm, "mid": v(-22.3, 21.16) * mm, "end": v(-22.63, 20.8) * mm});
            skArc(sketch, "E58.trimOffspring", {"start": v(-19.59, 23.69) * mm, "mid": v(-19.96, 23.37) * mm, "end": v(-20.33, 23.05) * mm});
            skArc(sketch, "E59.trimOffspring", {"start": v(-17, 25.6) * mm, "mid": v(-17.4, 25.33) * mm, "end": v(-17.8, 25.05) * mm});
            skArc(sketch, "E60.trimOffspring", {"start": v(-14.23, 27.24) * mm, "mid": v(-14.66, 27) * mm, "end": v(-15.1, 26.77) * mm});
            skArc(sketch, "E61.trimOffspring", {"start": v(-11.3, 28.58) * mm, "mid": v(-11.76, 28.4) * mm, "end": v(-12.21, 28.2) * mm});
            skArc(sketch, "E62.trimOffspring", {"start": v(-8.26, 29.6) * mm, "mid": v(-8.73, 29.47) * mm, "end": v(-9.2, 29.33) * mm});
            skArc(sketch, "E63.trimOffspring", {"start": v(-5.12, 30.3) * mm, "mid": v(-5.6, 30.22) * mm, "end": v(-6.08, 30.13) * mm});
            skArc(sketch, "E64.trimOffspring", {"start": v(-1.92, 30.67) * mm, "mid": v(-2.41, 30.64) * mm, "end": v(-2.9, 30.6) * mm});
            skSolve(sketch);
        }
        {
            var Q0;
            Q0 = qSketchRegion(id + "F0", true);
            extrude(context, id + "F1", {"entities" : qUnion([Q0]), "depth" : 6.35 * mm});
        }
        {
            var Q0;
            Q0=makeQuery(id+"F1.opExtrude","CAP_FACE",FACE,{"disambiguationData":[OSD([sQuery(id+"F0.wireOp",EDGE,"E0"),sQuery(id+"F0.wireOp",EDGE,"E1"),sQuery(id+"F0.wireOp",EDGE,"E2.trimOffspring"),sQuery(id+"F0.wireOp",EDGE,"E3.MirrorCS"),sQuery(id+"F0.wireOp",EDGE,"E4.MirrorCS"),sQuery(id+"F0.wireOp",EDGE,"E5.1.0"),sQuery(id+"F0.wireOp",EDGE,"E5.1.1"),sQuery(id+"F0.wireOp",EDGE,"E5.1.2"),sQuery(id+"F0.wireOp",EDGE,"E5.1.3"),sQuery(id+"F0.wireOp",EDGE,"E5.2.0"),sQuery(id+"F0.wireOp",EDGE,"E5.2.1"),sQuery(id+"F0.wireOp",EDGE,"E5.2.2"),sQuery(id+"F0.wireOp",EDGE,"E5.2.3"),sQuery(id+"F0.wireOp",EDGE,"E5.3.0"),sQuery(id+"F0.wireOp",EDGE,"E5.3.1"),sQuery(id+"F0.wireOp",EDGE,"E5.3.2"),sQuery(id+"F0.wireOp",EDGE,"E5.3.3"),sQuery(id+"F0.wireOp",EDGE,"E5.4.0"),sQuery(id+"F0.wireOp",EDGE,"E5.4.1"),sQuery(id+"F0.wireOp",EDGE,"E5.4.2"),sQuery(id+"F0.wireOp",EDGE,"E5.4.3"),sQuery(id+"F0.wireOp",EDGE,"E5.5.0"),sQuery(id+"F0.wireOp",EDGE,"E5.5.1"),sQuery(id+"F0.wireOp",EDGE,"E5.5.2"),sQuery(id+"F0.wireOp",EDGE,"E5.5.3"),sQuery(id+"F0.wireOp",EDGE,"E5.6.0"),sQuery(id+"F0.wireOp",EDGE,"E5.6.1"),sQuery(id+"F0.wireOp",EDGE,"E5.6.2"),sQuery(id+"F0.wireOp",EDGE,"E5.6.3"),sQuery(id+"F0.wireOp",EDGE,"E5.7.0"),sQuery(id+"F0.wireOp",EDGE,"E5.7.1"),sQuery(id+"F0.wireOp",EDGE,"E5.7.2"),sQuery(id+"F0.wireOp",EDGE,"E5.7.3"),sQuery(id+"F0.wireOp",EDGE,"E5.8.0"),sQuery(id+"F0.wireOp",EDGE,"E5.8.1"),sQuery(id+"F0.wireOp",EDGE,"E5.8.2"),sQuery(id+"F0.wireOp",EDGE,"E5.8.3"),sQuery(id+"F0.wireOp",EDGE,"E5.9.0"),sQuery(id+"F0.wireOp",EDGE,"E5.9.1"),sQuery(id+"F0.wireOp",EDGE,"E5.9.2"),sQuery(id+"F0.wireOp",EDGE,"E5.9.3"),sQuery(id+"F0.wireOp",EDGE,"E5.10.0"),sQuery(id+"F0.wireOp",EDGE,"E5.10.1"),sQuery(id+"F0.wireOp",EDGE,"E5.10.2"),sQuery(id+"F0.wireOp",EDGE,"E5.10.3"),sQuery(id+"F0.wireOp",EDGE,"E5.11.0"),sQuery(id+"F0.wireOp",EDGE,"E5.11.1"),sQuery(id+"F0.wireOp",EDGE,"E5.11.2"),sQuery(id+"F0.wireOp",EDGE,"E5.11.3"),sQuery(id+"F0.wireOp",EDGE,"E5.12.0"),sQuery(id+"F0.wireOp",EDGE,"E5.12.1"),sQuery(id+"F0.wireOp",EDGE,"E5.12.2"),sQuery(id+"F0.wireOp",EDGE,"E5.12.3"),sQuery(id+"F0.wireOp",EDGE,"E5.13.0"),sQuery(id+"F0.wireOp",EDGE,"E5.13.1"),sQuery(id+"F0.wireOp",EDGE,"E5.13.2"),sQuery(id+"F0.wireOp",EDGE,"E5.13.3"),sQuery(id+"F0.wireOp",EDGE,"E5.14.0"),sQuery(id+"F0.wireOp",EDGE,"E5.14.1"),sQuery(id+"F0.wireOp",EDGE,"E5.14.2"),sQuery(id+"F0.wireOp",EDGE,"E5.14.3"),sQuery(id+"F0.wireOp",EDGE,"E5.15.0"),sQuery(id+"F0.wireOp",EDGE,"E5.15.1"),sQuery(id+"F0.wireOp",EDGE,"E5.15.2"),sQuery(id+"F0.wireOp",EDGE,"E5.15.3"),sQuery(id+"F0.wireOp",EDGE,"E5.16.0"),sQuery(id+"F0.wireOp",EDGE,"E5.16.1"),sQuery(id+"F0.wireOp",EDGE,"E5.16.2"),sQuery(id+"F0.wireOp",EDGE,"E5.16.3"),sQuery(id+"F0.wireOp",EDGE,"E5.17.0"),sQuery(id+"F0.wireOp",EDGE,"E5.17.1"),sQuery(id+"F0.wireOp",EDGE,"E5.17.2"),sQuery(id+"F0.wireOp",EDGE,"E5.17.3"),sQuery(id+"F0.wireOp",EDGE,"E5.18.0"),sQuery(id+"F0.wireOp",EDGE,"E5.18.1"),sQuery(id+"F0.wireOp",EDGE,"E5.18.2"),sQuery(id+"F0.wireOp",EDGE,"E5.18.3"),sQuery(id+"F0.wireOp",EDGE,"E5.19.0"),sQuery(id+"F0.wireOp",EDGE,"E5.19.1"),sQuery(id+"F0.wireOp",EDGE,"E5.19.2"),sQuery(id+"F0.wireOp",EDGE,"E5.19.3"),sQuery(id+"F0.wireOp",EDGE,"E5.20.0"),sQuery(id+"F0.wireOp",EDGE,"E5.20.1"),sQuery(id+"F0.wireOp",EDGE,"E5.20.2"),sQuery(id+"F0.wireOp",EDGE,"E5.20.3"),sQuery(id+"F0.wireOp",EDGE,"E5.21.0"),sQuery(id+"F0.wireOp",EDGE,"E5.21.1"),sQuery(id+"F0.wireOp",EDGE,"E5.21.2"),sQuery(id+"F0.wireOp",EDGE,"E5.21.3"),sQuery(id+"F0.wireOp",EDGE,"E5.22.0"),sQuery(id+"F0.wireOp",EDGE,"E5.22.1"),sQuery(id+"F0.wireOp",EDGE,"E5.22.2"),sQuery(id+"F0.wireOp",EDGE,"E5.22.3"),sQuery(id+"F0.wireOp",EDGE,"E5.23.0"),sQuery(id+"F0.wireOp",EDGE,"E5.23.1"),sQuery(id+"F0.wireOp",EDGE,"E5.23.2"),sQuery(id+"F0.wireOp",EDGE,"E5.23.3"),sQuery(id+"F0.wireOp",EDGE,"E5.24.0"),sQuery(id+"F0.wireOp",EDGE,"E5.24.1"),sQuery(id+"F0.wireOp",EDGE,"E5.24.2"),sQuery(id+"F0.wireOp",EDGE,"E5.24.3"),sQuery(id+"F0.wireOp",EDGE,"E5.25.0"),sQuery(id+"F0.wireOp",EDGE,"E5.25.1"),sQuery(id+"F0.wireOp",EDGE,"E5.25.2"),sQuery(id+"F0.wireOp",EDGE,"E5.25.3"),sQuery(id+"F0.wireOp",EDGE,"E5.26.0"),sQuery(id+"F0.wireOp",EDGE,"E5.26.1"),sQuery(id+"F0.wireOp",EDGE,"E5.26.2"),sQuery(id+"F0.wireOp",EDGE,"E5.26.3"),sQuery(id+"F0.wireOp",EDGE,"E5.27.0"),sQuery(id+"F0.wireOp",EDGE,"E5.27.1"),sQuery(id+"F0.wireOp",EDGE,"E5.27.2"),sQuery(id+"F0.wireOp",EDGE,"E5.27.3"),sQuery(id+"F0.wireOp",EDGE,"E5.28.0"),sQuery(id+"F0.wireOp",EDGE,"E5.28.1"),sQuery(id+"F0.wireOp",EDGE,"E5.28.2"),sQuery(id+"F0.wireOp",EDGE,"E5.28.3"),sQuery(id+"F0.wireOp",EDGE,"E5.29.0"),sQuery(id+"F0.wireOp",EDGE,"E5.29.1"),sQuery(id+"F0.wireOp",EDGE,"E5.29.2"),sQuery(id+"F0.wireOp",EDGE,"E5.29.3"),sQuery(id+"F0.wireOp",EDGE,"E5.30.0"),sQuery(id+"F0.wireOp",EDGE,"E5.30.1"),sQuery(id+"F0.wireOp",EDGE,"E5.30.2"),sQuery(id+"F0.wireOp",EDGE,"E5.30.3"),sQuery(id+"F0.wireOp",EDGE,"E5.31.0"),sQuery(id+"F0.wireOp",EDGE,"E5.31.1"),sQuery(id+"F0.wireOp",EDGE,"E5.31.2"),sQuery(id+"F0.wireOp",EDGE,"E5.31.3"),sQuery(id+"F0.wireOp",EDGE,"E5.32.0"),sQuery(id+"F0.wireOp",EDGE,"E5.32.1"),sQuery(id+"F0.wireOp",EDGE,"E5.32.2"),sQuery(id+"F0.wireOp",EDGE,"E5.32.3"),sQuery(id+"F0.wireOp",EDGE,"E5.33.0"),sQuery(id+"F0.wireOp",EDGE,"E5.33.1"),sQuery(id+"F0.wireOp",EDGE,"E5.33.2"),sQuery(id+"F0.wireOp",EDGE,"E5.33.3"),sQuery(id+"F0.wireOp",EDGE,"E5.34.0"),sQuery(id+"F0.wireOp",EDGE,"E5.34.1"),sQuery(id+"F0.wireOp",EDGE,"E5.34.2"),sQuery(id+"F0.wireOp",EDGE,"E5.34.3"),sQuery(id+"F0.wireOp",EDGE,"E5.35.0"),sQuery(id+"F0.wireOp",EDGE,"E5.35.1"),sQuery(id+"F0.wireOp",EDGE,"E5.35.2"),sQuery(id+"F0.wireOp",EDGE,"E5.35.3"),sQuery(id+"F0.wireOp",EDGE,"E5.36.0"),sQuery(id+"F0.wireOp",EDGE,"E5.36.1"),sQuery(id+"F0.wireOp",EDGE,"E5.36.2"),sQuery(id+"F0.wireOp",EDGE,"E5.36.3"),sQuery(id+"F0.wireOp",EDGE,"E5.37.0"),sQuery(id+"F0.wireOp",EDGE,"E5.37.1"),sQuery(id+"F0.wireOp",EDGE,"E5.37.2"),sQuery(id+"F0.wireOp",EDGE,"E5.37.3"),sQuery(id+"F0.wireOp",EDGE,"E5.38.0"),sQuery(id+"F0.wireOp",EDGE,"E5.38.1"),sQuery(id+"F0.wireOp",EDGE,"E5.38.2"),sQuery(id+"F0.wireOp",EDGE,"E5.38.3"),sQuery(id+"F0.wireOp",EDGE,"E5.39.0"),sQuery(id+"F0.wireOp",EDGE,"E5.39.1"),sQuery(id+"F0.wireOp",EDGE,"E5.39.2"),sQuery(id+"F0.wireOp",EDGE,"E5.39.3"),sQuery(id+"F0.wireOp",EDGE,"E5.40.0"),sQuery(id+"F0.wireOp",EDGE,"E5.40.1"),sQuery(id+"F0.wireOp",EDGE,"E5.40.2"),sQuery(id+"F0.wireOp",EDGE,"E5.40.3"),sQuery(id+"F0.wireOp",EDGE,"E5.41.0"),sQuery(id+"F0.wireOp",EDGE,"E5.41.1"),sQuery(id+"F0.wireOp",EDGE,"E5.41.2"),sQuery(id+"F0.wireOp",EDGE,"E5.41.3"),sQuery(id+"F0.wireOp",EDGE,"E5.42.0"),sQuery(id+"F0.wireOp",EDGE,"E5.42.1"),sQuery(id+"F0.wireOp",EDGE,"E5.42.2"),sQuery(id+"F0.wireOp",EDGE,"E5.42.3"),sQuery(id+"F0.wireOp",EDGE,"E5.43.0"),sQuery(id+"F0.wireOp",EDGE,"E5.43.1"),sQuery(id+"F0.wireOp",EDGE,"E5.43.2"),sQuery(id+"F0.wireOp",EDGE,"E5.43.3"),sQuery(id+"F0.wireOp",EDGE,"E5.44.0"),sQuery(id+"F0.wireOp",EDGE,"E5.44.1"),sQuery(id+"F0.wireOp",EDGE,"E5.44.2"),sQuery(id+"F0.wireOp",EDGE,"E5.44.3"),sQuery(id+"F0.wireOp",EDGE,"E5.45.0"),sQuery(id+"F0.wireOp",EDGE,"E5.45.1"),sQuery(id+"F0.wireOp",EDGE,"E5.45.2"),sQuery(id+"F0.wireOp",EDGE,"E5.45.3"),sQuery(id+"F0.wireOp",EDGE,"E5.46.0"),sQuery(id+"F0.wireOp",EDGE,"E5.46.1"),sQuery(id+"F0.wireOp",EDGE,"E5.46.2"),sQuery(id+"F0.wireOp",EDGE,"E5.46.3"),sQuery(id+"F0.wireOp",EDGE,"E5.47.0"),sQuery(id+"F0.wireOp",EDGE,"E5.47.1"),sQuery(id+"F0.wireOp",EDGE,"E5.47.2"),sQuery(id+"F0.wireOp",EDGE,"E5.47.3"),sQuery(id+"F0.wireOp",EDGE,"E5.48.0"),sQuery(id+"F0.wireOp",EDGE,"E5.48.1"),sQuery(id+"F0.wireOp",EDGE,"E5.48.2"),sQuery(id+"F0.wireOp",EDGE,"E5.48.3"),sQuery(id+"F0.wireOp",EDGE,"E5.49.0"),sQuery(id+"F0.wireOp",EDGE,"E5.49.1"),sQuery(id+"F0.wireOp",EDGE,"E5.49.2"),sQuery(id+"F0.wireOp",EDGE,"E5.49.3"),sQuery(id+"F0.wireOp",EDGE,"E5.50.0"),sQuery(id+"F0.wireOp",EDGE,"E5.50.1"),sQuery(id+"F0.wireOp",EDGE,"E5.50.2"),sQuery(id+"F0.wireOp",EDGE,"E5.50.3"),sQuery(id+"F0.wireOp",EDGE,"E5.51.0"),sQuery(id+"F0.wireOp",EDGE,"E5.51.1"),sQuery(id+"F0.wireOp",EDGE,"E5.51.2"),sQuery(id+"F0.wireOp",EDGE,"E5.51.3"),sQuery(id+"F0.wireOp",EDGE,"E5.52.0"),sQuery(id+"F0.wireOp",EDGE,"E5.52.1"),sQuery(id+"F0.wireOp",EDGE,"E5.52.2"),sQuery(id+"F0.wireOp",EDGE,"E5.52.3"),sQuery(id+"F0.wireOp",EDGE,"E5.53.0"),sQuery(id+"F0.wireOp",EDGE,"E5.53.1"),sQuery(id+"F0.wireOp",EDGE,"E5.53.2"),sQuery(id+"F0.wireOp",EDGE,"E5.53.3"),sQuery(id+"F0.wireOp",EDGE,"E5.54.0"),sQuery(id+"F0.wireOp",EDGE,"E5.54.1"),sQuery(id+"F0.wireOp",EDGE,"E5.54.2"),sQuery(id+"F0.wireOp",EDGE,"E5.54.3"),sQuery(id+"F0.wireOp",EDGE,"E5.55.0"),sQuery(id+"F0.wireOp",EDGE,"E5.55.1"),sQuery(id+"F0.wireOp",EDGE,"E5.55.2"),sQuery(id+"F0.wireOp",EDGE,"E5.55.3"),sQuery(id+"F0.wireOp",EDGE,"E5.56.0"),sQuery(id+"F0.wireOp",EDGE,"E5.56.1"),sQuery(id+"F0.wireOp",EDGE,"E5.56.2"),sQuery(id+"F0.wireOp",EDGE,"E5.56.3"),sQuery(id+"F0.wireOp",EDGE,"E5.57.0"),sQuery(id+"F0.wireOp",EDGE,"E5.57.1"),sQuery(id+"F0.wireOp",EDGE,"E5.57.2"),sQuery(id+"F0.wireOp",EDGE,"E5.57.3"),sQuery(id+"F0.wireOp",EDGE,"E5.58.0"),sQuery(id+"F0.wireOp",EDGE,"E5.58.1"),sQuery(id+"F0.wireOp",EDGE,"E5.58.2"),sQuery(id+"F0.wireOp",EDGE,"E5.58.3"),sQuery(id+"F0.wireOp",EDGE,"E5.59.0"),sQuery(id+"F0.wireOp",EDGE,"E5.59.1"),sQuery(id+"F0.wireOp",EDGE,"E5.59.2"),sQuery(id+"F0.wireOp",EDGE,"E5.59.3"),sQuery(id+"F0.wireOp",EDGE,"E6.trimOffspring"),sQuery(id+"F0.wireOp",EDGE,"E7.trimOffspring"),sQuery(id+"F0.wireOp",EDGE,"E8.trimOffspring"),sQuery(id+"F0.wireOp",EDGE,"E9.trimOffspring"),sQuery(id+"F0.wireOp",EDGE,"E10.trimOffspring"),sQuery(id+"F0.wireOp",EDGE,"E11.trimOffspring"),sQuery(id+"F0.wireOp",EDGE,"E12.trimOffspring"),sQuery(id+"F0.wireOp",EDGE,"E13.trimOffspring"),sQuery(id+"F0.wireOp",EDGE,"E14.trimOffspring"),sQuery(id+"F0.wireOp",EDGE,"E15.trimOffspring"),sQuery(id+"F0.wireOp",EDGE,"E16.trimOffspring"),sQuery(id+"F0.wireOp",EDGE,"E17.trimOffspring"),sQuery(id+"F0.wireOp",EDGE,"E18.trimOffspring"),sQuery(id+"F0.wireOp",EDGE,"E19.trimOffspring"),sQuery(id+"F0.wireOp",EDGE,"E20.trimOffspring"),sQuery(id+"F0.wireOp",EDGE,"E21.trimOffspring"),sQuery(id+"F0.wireOp",EDGE,"E22.trimOffspring"),sQuery(id+"F0.wireOp",EDGE,"E23.trimOffspring"),sQuery(id+"F0.wireOp",EDGE,"E24.trimOffspring"),sQuery(id+"F0.wireOp",EDGE,"E25.trimOffspring"),sQuery(id+"F0.wireOp",EDGE,"E26.trimOffspring"),sQuery(id+"F0.wireOp",EDGE,"E27.trimOffspring"),sQuery(id+"F0.wireOp",EDGE,"E28.trimOffspring"),sQuery(id+"F0.wireOp",EDGE,"E29.trimOffspring"),sQuery(id+"F0.wireOp",EDGE,"E30.trimOffspring"),sQuery(id+"F0.wireOp",EDGE,"E31.trimOffspring"),sQuery(id+"F0.wireOp",EDGE,"E32"),sQuery(id+"F0.wireOp",EDGE,"E33.trimOffspring"),sQuery(id+"F0.wireOp",EDGE,"E34.trimOffspring"),sQuery(id+"F0.wireOp",EDGE,"E35.trimOffspring"),sQuery(id+"F0.wireOp",EDGE,"E36.trimOffspring"),sQuery(id+"F0.wireOp",EDGE,"E37.trimOffspring"),sQuery(id+"F0.wireOp",EDGE,"E38.trimOffspring"),sQuery(id+"F0.wireOp",EDGE,"E39.trimOffspring"),sQuery(id+"F0.wireOp",EDGE,"E40.trimOffspring"),sQuery(id+"F0.wireOp",EDGE,"E41.trimOffspring"),sQuery(id+"F0.wireOp",EDGE,"E42.trimOffspring"),sQuery(id+"F0.wireOp",EDGE,"E43.trimOffspring"),sQuery(id+"F0.wireOp",EDGE,"E44.trimOffspring"),sQuery(id+"F0.wireOp",EDGE,"E45.trimOffspring"),sQuery(id+"F0.wireOp",EDGE,"E46.trimOffspring"),sQuery(id+"F0.wireOp",EDGE,"E47.trimOffspring"),sQuery(id+"F0.wireOp",EDGE,"E48.trimOffspring"),sQuery(id+"F0.wireOp",EDGE,"E49.trimOffspring"),sQuery(id+"F0.wireOp",EDGE,"E50.trimOffspring"),sQuery(id+"F0.wireOp",EDGE,"E51.trimOffspring"),sQuery(id+"F0.wireOp",EDGE,"E52.trimOffspring"),sQuery(id+"F0.wireOp",EDGE,"E53.trimOffspring"),sQuery(id+"F0.wireOp",EDGE,"E54.trimOffspring"),sQuery(id+"F0.wireOp",EDGE,"E55.trimOffspring"),sQuery(id+"F0.wireOp",EDGE,"E56.trimOffspring"),sQuery(id+"F0.wireOp",EDGE,"E57.trimOffspring"),sQuery(id+"F0.wireOp",EDGE,"E58.trimOffspring"),sQuery(id+"F0.wireOp",EDGE,"E59.trimOffspring"),sQuery(id+"F0.wireOp",EDGE,"E60.trimOffspring"),sQuery(id+"F0.wireOp",EDGE,"E61.trimOffspring"),sQuery(id+"F0.wireOp",EDGE,"E62.trimOffspring"),sQuery(id+"F0.wireOp",EDGE,"E63.trimOffspring"),sQuery(id+"F0.wireOp",EDGE,"E64.trimOffspring")])],"isStart":false});
            var sketch = newSketch(context, id + "F2", { "sketchPlane" : qUnion([Q0])});
            skCircle(sketch, "E65", {"center": v(0, 0) * mm, "radius": 11.43 * mm});
            skSolve(sketch);
        }
        {
            var Q0;
            Q0=makeQuery(id+"F2.imprint","IMPRINT",FACE,{"disambiguationData":[TD([[makeQuery(id+"F2.imprint","IMPRINT",EDGE,{"derivedFrom":sQuery(id+"F2.wireOp",EDGE,"E65")}),1.0]])]});
            extrude(context, id + "F3", {"entities" : qUnion([Q0]), "operationType" : NewBodyOperationType.ADD, "depth" : 7.37 * mm});
        }
        {
            var Q0;
            Q0=makeQuery(id+"F3.opExtrude","CAP_FACE",FACE,{"disambiguationData":[OSD([sQuery(id+"F2.wireOp",EDGE,"E65")])],"isStart":false});
            var sketch = newSketch(context, id + "F4", { "sketchPlane" : qUnion([Q0])});
            skCircle(sketch, "E66.cCircle", {"center": v(0, 0) * mm, "radius": 6.45 * mm, "construction": true});
            skLineSegment(sketch, "E66.0", {"start": v(-3.27, 5.57) * mm, "end": v(3.19, 5.61) * mm});
            skLineSegment(sketch, "E66.1", {"start": v(3.19, 5.61) * mm, "end": v(6.45, 0.04) * mm});
            skLineSegment(sketch, "E66.2", {"start": v(6.45, 0.04) * mm, "end": v(3.27, -5.57) * mm});
            skLineSegment(sketch, "E66.3", {"start": v(3.27, -5.57) * mm, "end": v(-3.19, -5.61) * mm});
            skLineSegment(sketch, "E66.4", {"start": v(-3.19, -5.61) * mm, "end": v(-6.45, -0.04) * mm});
            skLineSegment(sketch, "E66.5", {"start": v(-6.45, -0.04) * mm, "end": v(-3.27, 5.57) * mm});
            skSolve(sketch);
        }
        {
            var Q0;
            Q0=makeQuery(id+"F4.imprint","IMPRINT",FACE,{"disambiguationData":[TD([[makeQuery(id+"F4.imprint","IMPRINT",EDGE,{"derivedFrom":sQuery(id+"F4.wireOp",EDGE,"E66.0")}),-1.0]])]});
            extrude(context, id + "F5", {"entities" : qUnion([Q0]), "operationType" : NewBodyOperationType.REMOVE, "oppositeDirection" : true, "depth" : 254 * mm});
        }
    });
